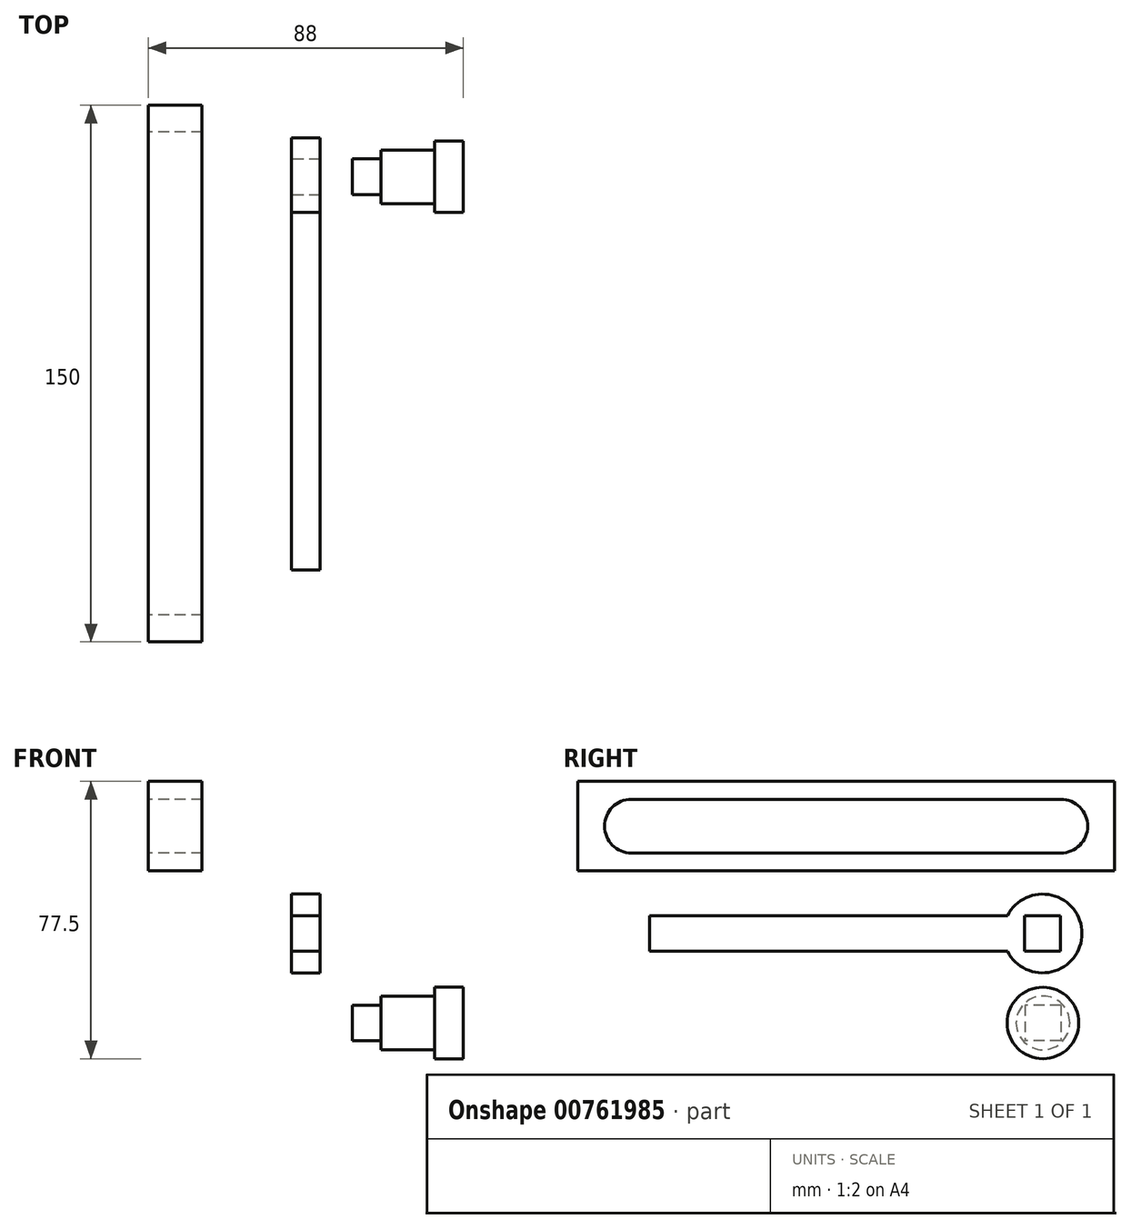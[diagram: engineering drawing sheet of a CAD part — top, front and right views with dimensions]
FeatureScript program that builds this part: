
annotation { "Feature Type Name" : "Feature", "Feature Type Description" : "" }
export const myFeature = defineFeature(function(context is Context, id is Id, definition is map)
    precondition{}
    {
        {
            var Q0;
            Q0=qCreatedBy(makeId("Right.planeOp"),FACE);
            var sketch = newSketch(context, id + "F0", { "sketchPlane" : qUnion([Q0])});
            skLineSegment(sketch, "E0.bottom", {"start": v(75, 12.5) * mm, "end": v(-75, 12.5) * mm});
            skLineSegment(sketch, "E0.top", {"start": v(75, -12.5) * mm, "end": v(-75, -12.5) * mm});
            skLineSegment(sketch, "E0.left", {"start": v(75, 12.5) * mm, "end": v(75, -12.5) * mm});
            skLineSegment(sketch, "E0.right", {"start": v(-75, 12.5) * mm, "end": v(-75, -12.5) * mm});
            skPoint(sketch, "E0.middle", {"position": v(0, 0) * mm});
            skLineSegment(sketch, "E1.bottom", {"start": v(60, 7.5) * mm, "end": v(-60, 7.5) * mm});
            skLineSegment(sketch, "E1.top", {"start": v(60, -7.5) * mm, "end": v(-60, -7.5) * mm});
            skLineSegment(sketch, "E1.left", {"start": v(60, 7.5) * mm, "end": v(60, -7.5) * mm, "construction": true});
            skLineSegment(sketch, "E1.right", {"start": v(-60, 7.5) * mm, "end": v(-60, -7.5) * mm, "construction": true});
            skArc(sketch, "E2", {"start": v(60, -7.5) * mm, "mid": v(67.5, 0) * mm, "end": v(60, 7.5) * mm});
            skArc(sketch, "E3", {"start": v(-60, 7.5) * mm, "mid": v(-67.5, 0) * mm, "end": v(-60, -7.5) * mm});
            skSolve(sketch);
        }
        {
            var Q0;
            Q0 = qSketchRegion(id + "F0", true);
            extrude(context, id + "F1", {"entities" : qUnion([Q0]), "depth" : 15 * mm, "offsetDistance" : 25 * mm});
        }
        {
            var Q0;
            Q0=qCreatedBy(makeId("Right.planeOp"),FACE);
            cPlane(context, id + "F2", {"entities" : qUnion([Q0]), "cplaneType" : CPlaneType.OFFSET, "offset" : 40 * mm, "width" : 150 * mm, "height" : 150 * mm});
        }
        {
            var Q0;
            Q0=qCreatedBy(id+"F2.planeOp",FACE);
            var sketch = newSketch(context, id + "F3", { "sketchPlane" : qUnion([Q0])});
            skLineSegment(sketch, "E4.bottom", {"start": v(45.1, -25) * mm, "end": v(-54.9, -25) * mm});
            skLineSegment(sketch, "E4.top", {"start": v(45.1, -35) * mm, "end": v(-54.9, -35) * mm});
            skLineSegment(sketch, "E4.right", {"start": v(-54.9, -25) * mm, "end": v(-54.9, -35) * mm});
            skPoint(sketch, "E4.middle", {"position": v(0, -30) * mm});
            skCircle(sketch, "E5", {"center": v(54.9, -30) * mm, "radius": 11 * mm});
            skPoint(sketch, "E6.orphan", {"position": v(54.9, -25) * mm});
            skPoint(sketch, "E7.orphan", {"position": v(54.9, -35) * mm});
            skLineSegment(sketch, "E8.bottom", {"start": v(59.9, -25) * mm, "end": v(49.9, -25) * mm});
            skLineSegment(sketch, "E8.top", {"start": v(59.9, -35) * mm, "end": v(49.9, -35) * mm});
            skLineSegment(sketch, "E8.left", {"start": v(59.9, -25) * mm, "end": v(59.9, -35) * mm});
            skLineSegment(sketch, "E8.right", {"start": v(49.9, -25) * mm, "end": v(49.9, -35) * mm});
            skSolve(sketch);
        }
        {
            var Q0;
            Q0 = qSketchRegion(id + "F3", true);
            extrude(context, id + "F4", {"entities" : qUnion([Q0]), "depth" : 8 * mm, "offsetDistance" : 25 * mm});
        }
        {
            var Q0;
            Q0=qCreatedBy(id+"F2.planeOp",FACE);
            cPlane(context, id + "F5", {"entities" : qUnion([Q0]), "cplaneType" : CPlaneType.OFFSET, "offset" : 40 * mm, "width" : 150 * mm, "height" : 150 * mm});
        }
        {
            var Q0;
            Q0=qCreatedBy(id+"F5.planeOp",FACE);
            var sketch = newSketch(context, id + "F6", { "sketchPlane" : qUnion([Q0])});
            skLineSegment(sketch, "E9.bottom", {"start": v(60, -50) * mm, "end": v(50, -50) * mm});
            skLineSegment(sketch, "E9.top", {"start": v(60, -60) * mm, "end": v(50, -60) * mm});
            skLineSegment(sketch, "E9.left", {"start": v(60, -50) * mm, "end": v(60, -60) * mm});
            skLineSegment(sketch, "E9.right", {"start": v(50, -50) * mm, "end": v(50, -60) * mm});
            skPoint(sketch, "E9.middle", {"position": v(55, -55) * mm});
            skCircle(sketch, "E10", {"center": v(55, -55) * mm, "radius": 7.5 * mm});
            skCircle(sketch, "E11", {"center": v(55, -55) * mm, "radius": 10 * mm});
            skSolve(sketch);
        }
        {
            var Q0;
            Q0=makeQuery(id+"F6.imprint","IMPRINT",FACE,{"disambiguationData":[TD([[makeQuery(id+"F6.imprint","IMPRINT",EDGE,{"derivedFrom":sQuery(id+"F6.wireOp",EDGE,"E9.bottom")}),-1.0]])]});
            var Q1;
            Q1=makeQuery(id+"F6.imprint","IMPRINT",FACE,{"disambiguationData":[TD([[makeQuery(id+"F6.imprint","IMPRINT",EDGE,{"derivedFrom":sQuery(id+"F6.wireOp",EDGE,"E9.bottom")}),1.0]])]});
            var Q2;
            Q2=makeQuery(id+"F6.imprint","IMPRINT",FACE,{"disambiguationData":[TD([[makeQuery(id+"F6.imprint","IMPRINT",EDGE,{"derivedFrom":sQuery(id+"F6.wireOp",EDGE,"E10")}),-1.0]])]});
            extrude(context, id + "F7", {"entities" : qUnion([Q0, Q1, Q2]), "depth" : 8 * mm, "offsetDistance" : 25 * mm});
        }
        {
            var Q0;
            Q0=makeQuery(id+"F6.imprint","IMPRINT",FACE,{"disambiguationData":[TD([[makeQuery(id+"F6.imprint","IMPRINT",EDGE,{"derivedFrom":sQuery(id+"F6.wireOp",EDGE,"E9.bottom")}),-1.0]])]});
            var Q1;
            Q1=makeQuery(id+"F6.imprint","IMPRINT",FACE,{"disambiguationData":[TD([[makeQuery(id+"F6.imprint","IMPRINT",EDGE,{"derivedFrom":sQuery(id+"F6.wireOp",EDGE,"E9.bottom")}),1.0]])]});
            extrude(context, id + "F8", {"entities" : qUnion([Q0, Q1]), "operationType" : NewBodyOperationType.ADD, "oppositeDirection" : true, "depth" : 15 * mm, "offsetDistance" : 25 * mm});
        }
        {
            var Q0;
            Q0=makeQuery(id+"F6.imprint","IMPRINT",FACE,{"disambiguationData":[TD([[makeQuery(id+"F6.imprint","IMPRINT",EDGE,{"derivedFrom":sQuery(id+"F6.wireOp",EDGE,"E9.bottom")}),1.0]])]});
            var Q1;
            Q1=sQuery(id+"F6.wireOp",EDGE,"E9.bottom");
            extrude(context, id + "F9", {"entities" : qUnion([Q0]), "operationType" : NewBodyOperationType.ADD, "surfaceEntities" : qUnion([Q1]), "oppositeDirection" : true, "depth" : 23 * mm, "offsetDistance" : 25 * mm});
        }
    });
